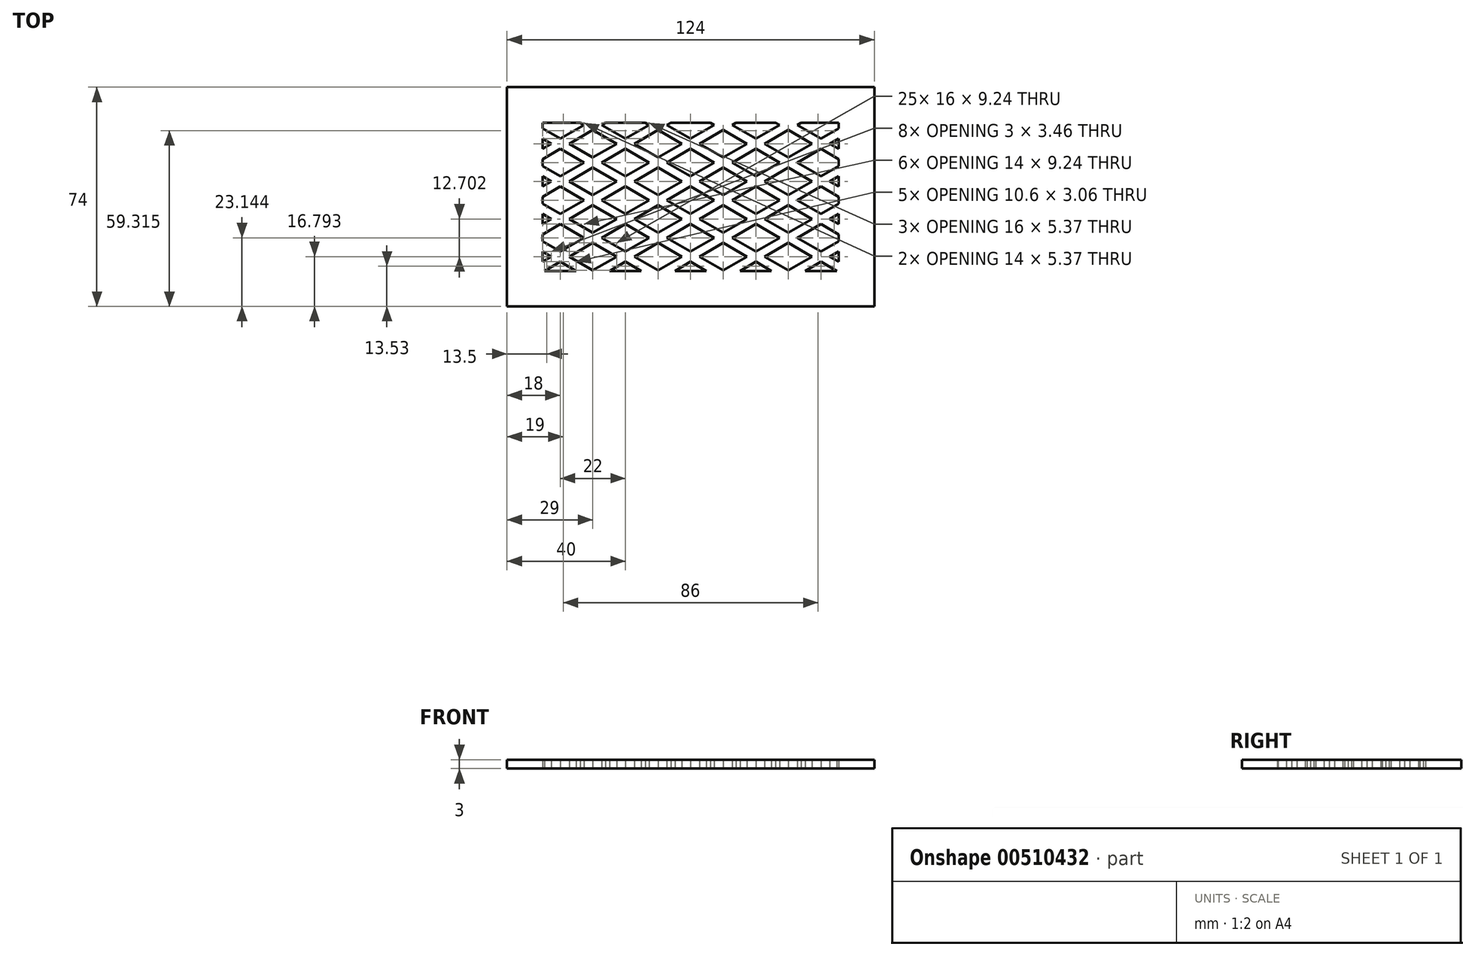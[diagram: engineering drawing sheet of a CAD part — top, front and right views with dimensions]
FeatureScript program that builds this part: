
annotation { "Feature Type Name" : "Feature", "Feature Type Description" : "" }
export const myFeature = defineFeature(function(context is Context, id is Id, definition is map)
    precondition{}
    {
        {
            var Q0;
            Q0=qCreatedBy(makeId("Top.planeOp"),FACE);
            var sketch = newSketch(context, id + "F0", { "sketchPlane" : qUnion([Q0])});
            skLineSegment(sketch, "E0.bottom", {"start": v(-62, 74) * mm, "end": v(62, 74) * mm});
            skLineSegment(sketch, "E0.top", {"start": v(-62, 0) * mm, "end": v(62, 0) * mm});
            skLineSegment(sketch, "E0.left", {"start": v(-62, 74) * mm, "end": v(-62, 0) * mm});
            skLineSegment(sketch, "E0.right", {"start": v(62, 74) * mm, "end": v(62, 0) * mm});
            skLineSegment(sketch, "E1", {"start": v(0, -17.07) * mm, "end": v(0, 81.23) * mm, "construction": true});
            skLineSegment(sketch, "E2.bottom", {"start": v(-50, 62) * mm, "end": v(-37.3, 62) * mm});
            skLineSegment(sketch, "E2.top", {"start": v(-49.3, 12) * mm, "end": v(-38.7, 12) * mm});
            skLineSegment(sketch, "E2.left", {"start": v(-50, 62) * mm, "end": v(-50, 60.1) * mm});
            skLineSegment(sketch, "E2.right", {"start": v(50, 62) * mm, "end": v(50, 60.1) * mm});
            skLineSegment(sketch, "E3", {"start": v(-50, 53.17) * mm, "end": v(-47, 54.9) * mm});
            skLineSegment(sketch, "E4", {"start": v(-50, 49.7) * mm, "end": v(-44, 53.17) * mm});
            skLineSegment(sketch, "E5", {"start": v(-50, 40.46) * mm, "end": v(-47, 42.2) * mm});
            skLineSegment(sketch, "E6", {"start": v(-50, 37) * mm, "end": v(-44, 40.46) * mm});
            skLineSegment(sketch, "E7", {"start": v(-50, 27.76) * mm, "end": v(-47, 29.5) * mm});
            skLineSegment(sketch, "E8", {"start": v(-50, 24.3) * mm, "end": v(-44, 27.76) * mm});
            skLineSegment(sketch, "E9", {"start": v(-50, 15.06) * mm, "end": v(-47, 16.8) * mm});
            skLineSegment(sketch, "E10", {"start": v(-49.3, 12) * mm, "end": v(-44, 15.06) * mm});
            skLineSegment(sketch, "E11", {"start": v(-33.3, 12) * mm, "end": v(-25, 16.8) * mm});
            skLineSegment(sketch, "E12", {"start": v(-27.3, 12) * mm, "end": v(-22, 15.06) * mm});
            skLineSegment(sketch, "E13", {"start": v(-11.3, 12) * mm, "end": v(-3, 16.8) * mm});
            skLineSegment(sketch, "E14", {"start": v(-5.3, 12) * mm, "end": v(0, 15.06) * mm});
            skLineSegment(sketch, "E15", {"start": v(10.7, 12) * mm, "end": v(19, 16.8) * mm});
            skLineSegment(sketch, "E16", {"start": v(16.7, 12) * mm, "end": v(22, 15.06) * mm});
            skLineSegment(sketch, "E17", {"start": v(32.7, 12) * mm, "end": v(41, 16.8) * mm});
            skLineSegment(sketch, "E18", {"start": v(38.7, 12) * mm, "end": v(44, 15.06) * mm});
            skLineSegment(sketch, "E19.MirrorCS", {"start": v(-32.7, 12) * mm, "end": v(-41, 16.8) * mm});
            skLineSegment(sketch, "E20.MirrorCS", {"start": v(-38.7, 12) * mm, "end": v(-44, 15.06) * mm});
            skLineSegment(sketch, "E21.MirrorCS", {"start": v(50, 49.7) * mm, "end": v(44, 53.17) * mm});
            skLineSegment(sketch, "E22.MirrorCS", {"start": v(50, 40.46) * mm, "end": v(47, 42.2) * mm});
            skLineSegment(sketch, "E23.MirrorCS", {"start": v(49.3, 12) * mm, "end": v(44, 15.06) * mm});
            skLineSegment(sketch, "E24.MirrorCS", {"start": v(-10.7, 12) * mm, "end": v(-19, 16.8) * mm});
            skLineSegment(sketch, "E25.MirrorCS", {"start": v(50, 15.06) * mm, "end": v(47, 16.8) * mm});
            skLineSegment(sketch, "E26.MirrorCS", {"start": v(33.3, 12) * mm, "end": v(25, 16.8) * mm});
            skLineSegment(sketch, "E27.MirrorCS", {"start": v(50, 27.76) * mm, "end": v(47, 29.5) * mm});
            skLineSegment(sketch, "E28.MirrorCS", {"start": v(50, 53.17) * mm, "end": v(47, 54.9) * mm});
            skLineSegment(sketch, "E29.MirrorCS", {"start": v(50, 37) * mm, "end": v(44, 40.46) * mm});
            skLineSegment(sketch, "E30.MirrorCS", {"start": v(50, 24.3) * mm, "end": v(44, 27.76) * mm});
            skLineSegment(sketch, "E31.MirrorCS", {"start": v(5.3, 12) * mm, "end": v(0, 15.06) * mm});
            skLineSegment(sketch, "E32.MirrorCS", {"start": v(11.3, 12) * mm, "end": v(3, 16.8) * mm});
            skLineSegment(sketch, "E33.MirrorCS", {"start": v(27.3, 12) * mm, "end": v(22, 15.06) * mm});
            skLineSegment(sketch, "E34.MirrorCS", {"start": v(-16.7, 12) * mm, "end": v(-22, 15.06) * mm});
            skLineSegment(sketch, "E35", {"start": v(50, 53.17) * mm, "end": v(50, 49.7) * mm});
            skLineSegment(sketch, "E36", {"start": v(50, 34.7) * mm, "end": v(50, 31.23) * mm});
            skLineSegment(sketch, "E37.trimOffspring", {"start": v(-30, 48.55) * mm, "end": v(-22, 53.17) * mm});
            skLineSegment(sketch, "E38.trimOffspring", {"start": v(-33, 50.28) * mm, "end": v(-41, 54.9) * mm});
            skLineSegment(sketch, "E39.trimOffspring", {"start": v(-36, 48.55) * mm, "end": v(-44, 53.17) * mm});
            skLineSegment(sketch, "E40.trimOffspring", {"start": v(-33, 50.28) * mm, "end": v(-25, 54.9) * mm});
            skLineSegment(sketch, "E41.trimOffspring", {"start": v(-41, 54.9) * mm, "end": v(-33, 59.52) * mm});
            skLineSegment(sketch, "E42.trimOffspring", {"start": v(-44, 56.63) * mm, "end": v(-36, 61.25) * mm});
            skLineSegment(sketch, "E43.trimOffspring", {"start": v(-47, 54.9) * mm, "end": v(-50, 56.63) * mm});
            skLineSegment(sketch, "E44.trimOffspring", {"start": v(-44, 56.63) * mm, "end": v(-50, 60.1) * mm});
            skLineSegment(sketch, "E45.trimOffspring", {"start": v(-36, 61.25) * mm, "end": v(-37.3, 62) * mm});
            skLineSegment(sketch, "E46.trimOffspring", {"start": v(-30, 61.25) * mm, "end": v(-28.7, 62) * mm});
            skLineSegment(sketch, "E47.trimOffspring", {"start": v(-50, 56.63) * mm, "end": v(-50, 53.17) * mm});
            skLineSegment(sketch, "E48.trimOffspring", {"start": v(-50, 49.7) * mm, "end": v(-50, 47.4) * mm});
            skLineSegment(sketch, "E49.trimOffspring", {"start": v(-50, 43.93) * mm, "end": v(-50, 40.46) * mm});
            skLineSegment(sketch, "E50.trimOffspring", {"start": v(-50, 37) * mm, "end": v(-50, 34.7) * mm});
            skLineSegment(sketch, "E51.trimOffspring", {"start": v(-50, 31.23) * mm, "end": v(-50, 27.76) * mm});
            skLineSegment(sketch, "E52.trimOffspring", {"start": v(-50, 24.3) * mm, "end": v(-50, 21.99) * mm});
            skLineSegment(sketch, "E53.trimOffspring", {"start": v(-50, 18.52) * mm, "end": v(-50, 15.06) * mm});
            skPoint(sketch, "E54.end.orphan", {"position": v(-50, 12) * mm});
            skLineSegment(sketch, "E55.trimOffspring", {"start": v(-47, 29.5) * mm, "end": v(-50, 31.23) * mm});
            skLineSegment(sketch, "E56.trimOffspring", {"start": v(-44, 31.23) * mm, "end": v(-50, 34.7) * mm});
            skLineSegment(sketch, "E57.trimOffspring", {"start": v(-44, 31.23) * mm, "end": v(-36, 35.85) * mm});
            skLineSegment(sketch, "E58.trimOffspring", {"start": v(-41, 29.5) * mm, "end": v(-33, 34.11) * mm});
            skLineSegment(sketch, "E59.trimOffspring", {"start": v(-30, 35.85) * mm, "end": v(-22, 40.46) * mm});
            skLineSegment(sketch, "E60.trimOffspring", {"start": v(-33, 37.58) * mm, "end": v(-25, 42.2) * mm});
            skLineSegment(sketch, "E61.trimOffspring", {"start": v(-36, 35.85) * mm, "end": v(-44, 40.46) * mm});
            skLineSegment(sketch, "E62.trimOffspring", {"start": v(-33, 37.58) * mm, "end": v(-41, 42.2) * mm});
            skLineSegment(sketch, "E63.trimOffspring", {"start": v(-41, 42.2) * mm, "end": v(-33, 46.81) * mm});
            skLineSegment(sketch, "E64.trimOffspring", {"start": v(-47, 42.2) * mm, "end": v(-50, 43.93) * mm});
            skLineSegment(sketch, "E65.trimOffspring", {"start": v(-44, 43.93) * mm, "end": v(-36, 48.55) * mm});
            skLineSegment(sketch, "E66.trimOffspring", {"start": v(-44, 43.93) * mm, "end": v(-50, 47.4) * mm});
            skLineSegment(sketch, "E67.trimOffspring", {"start": v(-22, 43.93) * mm, "end": v(-14, 48.55) * mm});
            skLineSegment(sketch, "E68.trimOffspring", {"start": v(-25, 42.2) * mm, "end": v(-33, 46.81) * mm});
            skLineSegment(sketch, "E69.trimOffspring", {"start": v(-22, 43.93) * mm, "end": v(-30, 48.55) * mm});
            skLineSegment(sketch, "E70.trimOffspring", {"start": v(-19, 42.2) * mm, "end": v(-11, 46.81) * mm});
            skLineSegment(sketch, "E71.trimOffspring", {"start": v(-28.7, 62) * mm, "end": v(-15.3, 62) * mm});
            skLineSegment(sketch, "E72.trimOffspring", {"start": v(-22, 56.63) * mm, "end": v(-14, 61.25) * mm});
            skLineSegment(sketch, "E73.trimOffspring", {"start": v(-19, 54.9) * mm, "end": v(-11, 59.52) * mm});
            skLineSegment(sketch, "E74.trimOffspring", {"start": v(-22, 56.63) * mm, "end": v(-30, 61.25) * mm});
            skLineSegment(sketch, "E75.trimOffspring", {"start": v(-25, 54.9) * mm, "end": v(-33, 59.52) * mm});
            skLineSegment(sketch, "E76.trimOffspring", {"start": v(-14, 61.25) * mm, "end": v(-15.3, 62) * mm});
            skLineSegment(sketch, "E77.trimOffspring", {"start": v(-6.7, 62) * mm, "end": v(6.7, 62) * mm});
            skLineSegment(sketch, "E78.trimOffspring", {"start": v(-8, 61.25) * mm, "end": v(-6.7, 62) * mm});
            skLineSegment(sketch, "E79.trimOffspring", {"start": v(0, 56.63) * mm, "end": v(8, 61.25) * mm});
            skLineSegment(sketch, "E80.trimOffspring", {"start": v(0, 56.63) * mm, "end": v(-8, 61.25) * mm});
            skLineSegment(sketch, "E81.trimOffspring", {"start": v(3, 54.9) * mm, "end": v(11, 59.52) * mm});
            skLineSegment(sketch, "E82.trimOffspring", {"start": v(-3, 54.9) * mm, "end": v(-11, 59.52) * mm});
            skLineSegment(sketch, "E83.trimOffspring", {"start": v(-11, 50.28) * mm, "end": v(-19, 54.9) * mm});
            skLineSegment(sketch, "E84.trimOffspring", {"start": v(-11, 50.28) * mm, "end": v(-3, 54.9) * mm});
            skLineSegment(sketch, "E85.trimOffspring", {"start": v(-14, 48.55) * mm, "end": v(-22, 53.17) * mm});
            skLineSegment(sketch, "E86.trimOffspring", {"start": v(-8, 48.55) * mm, "end": v(0, 53.17) * mm});
            skLineSegment(sketch, "E87.trimOffspring", {"start": v(-33, 24.88) * mm, "end": v(-25, 29.5) * mm});
            skLineSegment(sketch, "E88.trimOffspring", {"start": v(-33, 24.88) * mm, "end": v(-41, 29.5) * mm});
            skLineSegment(sketch, "E89.trimOffspring", {"start": v(-30, 23.14) * mm, "end": v(-22, 27.76) * mm});
            skLineSegment(sketch, "E90.trimOffspring", {"start": v(-36, 23.14) * mm, "end": v(-44, 27.76) * mm});
            skLineSegment(sketch, "E91.trimOffspring", {"start": v(-44, 18.52) * mm, "end": v(-50, 21.99) * mm});
            skLineSegment(sketch, "E92.trimOffspring", {"start": v(-47, 16.8) * mm, "end": v(-50, 18.52) * mm});
            skLineSegment(sketch, "E93.trimOffspring", {"start": v(-44, 18.52) * mm, "end": v(-36, 23.14) * mm});
            skLineSegment(sketch, "E94.trimOffspring", {"start": v(-41, 16.8) * mm, "end": v(-33, 21.41) * mm});
            skLineSegment(sketch, "E95.trimOffspring", {"start": v(-27.3, 12) * mm, "end": v(-16.7, 12) * mm});
            skLineSegment(sketch, "E96.trimOffspring", {"start": v(-5.3, 12) * mm, "end": v(5.3, 12) * mm});
            skLineSegment(sketch, "E97.trimOffspring", {"start": v(-19, 16.8) * mm, "end": v(-11, 21.41) * mm});
            skLineSegment(sketch, "E98.trimOffspring", {"start": v(-25, 16.8) * mm, "end": v(-33, 21.41) * mm});
            skLineSegment(sketch, "E99.trimOffspring", {"start": v(-22, 18.52) * mm, "end": v(-14, 23.14) * mm});
            skLineSegment(sketch, "E100.trimOffspring", {"start": v(-22, 18.52) * mm, "end": v(-30, 23.14) * mm});
            skLineSegment(sketch, "E101.trimOffspring", {"start": v(-14, 23.14) * mm, "end": v(-22, 27.76) * mm});
            skLineSegment(sketch, "E102.trimOffspring", {"start": v(-11, 24.88) * mm, "end": v(-19, 29.5) * mm});
            skLineSegment(sketch, "E103.trimOffspring", {"start": v(-8, 23.14) * mm, "end": v(0, 27.76) * mm});
            skLineSegment(sketch, "E104.trimOffspring", {"start": v(-11, 24.88) * mm, "end": v(-3, 29.5) * mm});
            skLineSegment(sketch, "E105.trimOffspring", {"start": v(-19, 29.5) * mm, "end": v(-11, 34.11) * mm});
            skLineSegment(sketch, "E106.trimOffspring", {"start": v(-25, 29.5) * mm, "end": v(-33, 34.11) * mm});
            skLineSegment(sketch, "E107.trimOffspring", {"start": v(-22, 31.23) * mm, "end": v(-14, 35.85) * mm});
            skLineSegment(sketch, "E108.trimOffspring", {"start": v(-22, 31.23) * mm, "end": v(-30, 35.85) * mm});
            skLineSegment(sketch, "E109.trimOffspring", {"start": v(-14, 35.85) * mm, "end": v(-22, 40.46) * mm});
            skLineSegment(sketch, "E110.trimOffspring", {"start": v(-11, 37.58) * mm, "end": v(-3, 42.2) * mm});
            skLineSegment(sketch, "E111.trimOffspring", {"start": v(-8, 35.85) * mm, "end": v(0, 40.46) * mm});
            skLineSegment(sketch, "E112.trimOffspring", {"start": v(-11, 37.58) * mm, "end": v(-19, 42.2) * mm});
            skLineSegment(sketch, "E113.trimOffspring", {"start": v(0, 31.23) * mm, "end": v(8, 35.85) * mm});
            skLineSegment(sketch, "E114.trimOffspring", {"start": v(3, 29.5) * mm, "end": v(11, 34.11) * mm});
            skLineSegment(sketch, "E115.trimOffspring", {"start": v(0, 31.23) * mm, "end": v(-8, 35.85) * mm});
            skLineSegment(sketch, "E116.trimOffspring", {"start": v(-3, 29.5) * mm, "end": v(-11, 34.11) * mm});
            skLineSegment(sketch, "E117.trimOffspring", {"start": v(0, 43.93) * mm, "end": v(8, 48.55) * mm});
            skLineSegment(sketch, "E118.trimOffspring", {"start": v(-3, 42.2) * mm, "end": v(-11, 46.81) * mm});
            skLineSegment(sketch, "E119.trimOffspring", {"start": v(3, 42.2) * mm, "end": v(11, 46.81) * mm});
            skLineSegment(sketch, "E120.trimOffspring", {"start": v(0, 43.93) * mm, "end": v(-8, 48.55) * mm});
            skLineSegment(sketch, "E121.trimOffspring", {"start": v(15.3, 62) * mm, "end": v(28.7, 62) * mm});
            skLineSegment(sketch, "E122.trimOffspring", {"start": v(8, 61.25) * mm, "end": v(6.7, 62) * mm});
            skLineSegment(sketch, "E123.trimOffspring", {"start": v(14, 61.25) * mm, "end": v(15.3, 62) * mm});
            skLineSegment(sketch, "E124.trimOffspring", {"start": v(11, 50.28) * mm, "end": v(3, 54.9) * mm});
            skLineSegment(sketch, "E125.trimOffspring", {"start": v(11, 50.28) * mm, "end": v(19, 54.9) * mm});
            skLineSegment(sketch, "E126.trimOffspring", {"start": v(8, 48.55) * mm, "end": v(0, 53.17) * mm});
            skLineSegment(sketch, "E127.trimOffspring", {"start": v(14, 48.55) * mm, "end": v(22, 53.17) * mm});
            skLineSegment(sketch, "E128.trimOffspring", {"start": v(19, 54.9) * mm, "end": v(11, 59.52) * mm});
            skLineSegment(sketch, "E129.trimOffspring", {"start": v(22, 56.63) * mm, "end": v(30, 61.25) * mm});
            skLineSegment(sketch, "E130.trimOffspring", {"start": v(22, 56.63) * mm, "end": v(14, 61.25) * mm});
            skLineSegment(sketch, "E131.trimOffspring", {"start": v(25, 54.9) * mm, "end": v(33, 59.52) * mm});
            skLineSegment(sketch, "E132.trimOffspring", {"start": v(30, 61.25) * mm, "end": v(28.7, 62) * mm});
            skLineSegment(sketch, "E133.trimOffspring", {"start": v(36, 61.25) * mm, "end": v(37.3, 62) * mm});
            skLineSegment(sketch, "E134.trimOffspring", {"start": v(37.3, 62) * mm, "end": v(50, 62) * mm});
            skLineSegment(sketch, "E135.trimOffspring", {"start": v(50, 56.63) * mm, "end": v(50, 47.4) * mm});
            skLineSegment(sketch, "E136.trimOffspring", {"start": v(44, 56.63) * mm, "end": v(36, 61.25) * mm});
            skLineSegment(sketch, "E137.trimOffspring", {"start": v(41, 54.9) * mm, "end": v(33, 59.52) * mm});
            skLineSegment(sketch, "E138.trimOffspring", {"start": v(44, 56.63) * mm, "end": v(50, 60.1) * mm});
            skLineSegment(sketch, "E139.trimOffspring", {"start": v(47, 54.9) * mm, "end": v(50, 56.63) * mm});
            skLineSegment(sketch, "E140.trimOffspring", {"start": v(33, 50.28) * mm, "end": v(41, 54.9) * mm});
            skLineSegment(sketch, "E141.trimOffspring", {"start": v(33, 50.28) * mm, "end": v(25, 54.9) * mm});
            skLineSegment(sketch, "E142.trimOffspring", {"start": v(30, 48.55) * mm, "end": v(22, 53.17) * mm});
            skLineSegment(sketch, "E143.trimOffspring", {"start": v(36, 48.55) * mm, "end": v(44, 53.17) * mm});
            skLineSegment(sketch, "E144.trimOffspring", {"start": v(44, 43.93) * mm, "end": v(50, 47.4) * mm});
            skLineSegment(sketch, "E145.trimOffspring", {"start": v(44, 43.93) * mm, "end": v(36, 48.55) * mm});
            skLineSegment(sketch, "E146.trimOffspring", {"start": v(47, 42.2) * mm, "end": v(50, 43.93) * mm});
            skLineSegment(sketch, "E147.trimOffspring", {"start": v(41, 42.2) * mm, "end": v(33, 46.81) * mm});
            skLineSegment(sketch, "E148.trimOffspring", {"start": v(50, 43.93) * mm, "end": v(50, 40.46) * mm});
            skLineSegment(sketch, "E149.trimOffspring", {"start": v(50, 37) * mm, "end": v(50, 27.76) * mm});
            skLineSegment(sketch, "E150.trimOffspring", {"start": v(22, 43.93) * mm, "end": v(14, 48.55) * mm});
            skLineSegment(sketch, "E151.trimOffspring", {"start": v(22, 43.93) * mm, "end": v(30, 48.55) * mm});
            skLineSegment(sketch, "E152.trimOffspring", {"start": v(19, 42.2) * mm, "end": v(11, 46.81) * mm});
            skLineSegment(sketch, "E153.trimOffspring", {"start": v(25, 42.2) * mm, "end": v(33, 46.81) * mm});
            skLineSegment(sketch, "E154.trimOffspring", {"start": v(33, 37.58) * mm, "end": v(41, 42.2) * mm});
            skLineSegment(sketch, "E155.trimOffspring", {"start": v(30, 35.85) * mm, "end": v(22, 40.46) * mm});
            skLineSegment(sketch, "E156.trimOffspring", {"start": v(33, 37.58) * mm, "end": v(25, 42.2) * mm});
            skLineSegment(sketch, "E157.trimOffspring", {"start": v(36, 35.85) * mm, "end": v(44, 40.46) * mm});
            skLineSegment(sketch, "E158.trimOffspring", {"start": v(44, 31.23) * mm, "end": v(50, 34.7) * mm});
            skLineSegment(sketch, "E159.trimOffspring", {"start": v(44, 31.23) * mm, "end": v(36, 35.85) * mm});
            skLineSegment(sketch, "E160.trimOffspring", {"start": v(41, 29.5) * mm, "end": v(33, 34.11) * mm});
            skLineSegment(sketch, "E161.trimOffspring", {"start": v(47, 29.5) * mm, "end": v(50, 31.23) * mm});
            skLineSegment(sketch, "E162.trimOffspring", {"start": v(50, 24.3) * mm, "end": v(50, 21.99) * mm});
            skLineSegment(sketch, "E163.trimOffspring", {"start": v(11, 37.58) * mm, "end": v(3, 42.2) * mm});
            skLineSegment(sketch, "E164.trimOffspring", {"start": v(11, 37.58) * mm, "end": v(19, 42.2) * mm});
            skLineSegment(sketch, "E165.trimOffspring", {"start": v(8, 35.85) * mm, "end": v(0, 40.46) * mm});
            skLineSegment(sketch, "E166.trimOffspring", {"start": v(14, 35.85) * mm, "end": v(22, 40.46) * mm});
            skLineSegment(sketch, "E167.trimOffspring", {"start": v(22, 31.23) * mm, "end": v(30, 35.85) * mm});
            skLineSegment(sketch, "E168.trimOffspring", {"start": v(25, 29.5) * mm, "end": v(33, 34.11) * mm});
            skLineSegment(sketch, "E169.trimOffspring", {"start": v(22, 31.23) * mm, "end": v(14, 35.85) * mm});
            skLineSegment(sketch, "E170.trimOffspring", {"start": v(19, 29.5) * mm, "end": v(11, 34.11) * mm});
            skLineSegment(sketch, "E171.trimOffspring", {"start": v(11, 24.88) * mm, "end": v(3, 29.5) * mm});
            skLineSegment(sketch, "E172.trimOffspring", {"start": v(11, 24.88) * mm, "end": v(19, 29.5) * mm});
            skLineSegment(sketch, "E173.trimOffspring", {"start": v(8, 23.14) * mm, "end": v(0, 27.76) * mm});
            skLineSegment(sketch, "E174.trimOffspring", {"start": v(14, 23.14) * mm, "end": v(22, 27.76) * mm});
            skLineSegment(sketch, "E175.trimOffspring", {"start": v(0, 18.52) * mm, "end": v(8, 23.14) * mm});
            skLineSegment(sketch, "E176.trimOffspring", {"start": v(-3, 16.8) * mm, "end": v(-11, 21.41) * mm});
            skLineSegment(sketch, "E177.trimOffspring", {"start": v(3, 16.8) * mm, "end": v(11, 21.41) * mm});
            skLineSegment(sketch, "E178.trimOffspring", {"start": v(0, 18.52) * mm, "end": v(-8, 23.14) * mm});
            skLineSegment(sketch, "E179.trimOffspring", {"start": v(22, 18.52) * mm, "end": v(30, 23.14) * mm});
            skLineSegment(sketch, "E180.trimOffspring", {"start": v(19, 16.8) * mm, "end": v(11, 21.41) * mm});
            skLineSegment(sketch, "E181.trimOffspring", {"start": v(22, 18.52) * mm, "end": v(14, 23.14) * mm});
            skLineSegment(sketch, "E182.trimOffspring", {"start": v(25, 16.8) * mm, "end": v(33, 21.41) * mm});
            skLineSegment(sketch, "E183.trimOffspring", {"start": v(30, 23.14) * mm, "end": v(22, 27.76) * mm});
            skLineSegment(sketch, "E184.trimOffspring", {"start": v(33, 24.88) * mm, "end": v(25, 29.5) * mm});
            skLineSegment(sketch, "E185.trimOffspring", {"start": v(33, 24.88) * mm, "end": v(41, 29.5) * mm});
            skLineSegment(sketch, "E186.trimOffspring", {"start": v(36, 23.14) * mm, "end": v(44, 27.76) * mm});
            skLineSegment(sketch, "E187.trimOffspring", {"start": v(50, 18.52) * mm, "end": v(50, 15.06) * mm});
            skLineSegment(sketch, "E188.trimOffspring", {"start": v(47, 16.8) * mm, "end": v(50, 18.52) * mm});
            skLineSegment(sketch, "E189.trimOffspring", {"start": v(44, 18.52) * mm, "end": v(36, 23.14) * mm});
            skLineSegment(sketch, "E190.trimOffspring", {"start": v(44, 18.52) * mm, "end": v(50, 21.99) * mm});
            skLineSegment(sketch, "E191.trimOffspring", {"start": v(41, 16.8) * mm, "end": v(33, 21.41) * mm});
            skLineSegment(sketch, "E192.trimOffspring", {"start": v(38.7, 12) * mm, "end": v(49.3, 12) * mm});
            skLineSegment(sketch, "E193.trimOffspring", {"start": v(16.7, 12) * mm, "end": v(27.3, 12) * mm});
            skSolve(sketch);
        }
        {
            var Q0;
            Q0=makeQuery(id+"F0.imprint","IMPRINT",FACE,{"disambiguationData":[TD([[makeQuery(id+"F0.imprint","IMPRINT",EDGE,{"derivedFrom":sQuery(id+"F0.wireOp",EDGE,"E0.bottom")}),-1.0]])]});
            extrude(context, id + "F1", {"entities" : qUnion([Q0]), "depth" : 3 * mm});
        }
    });
